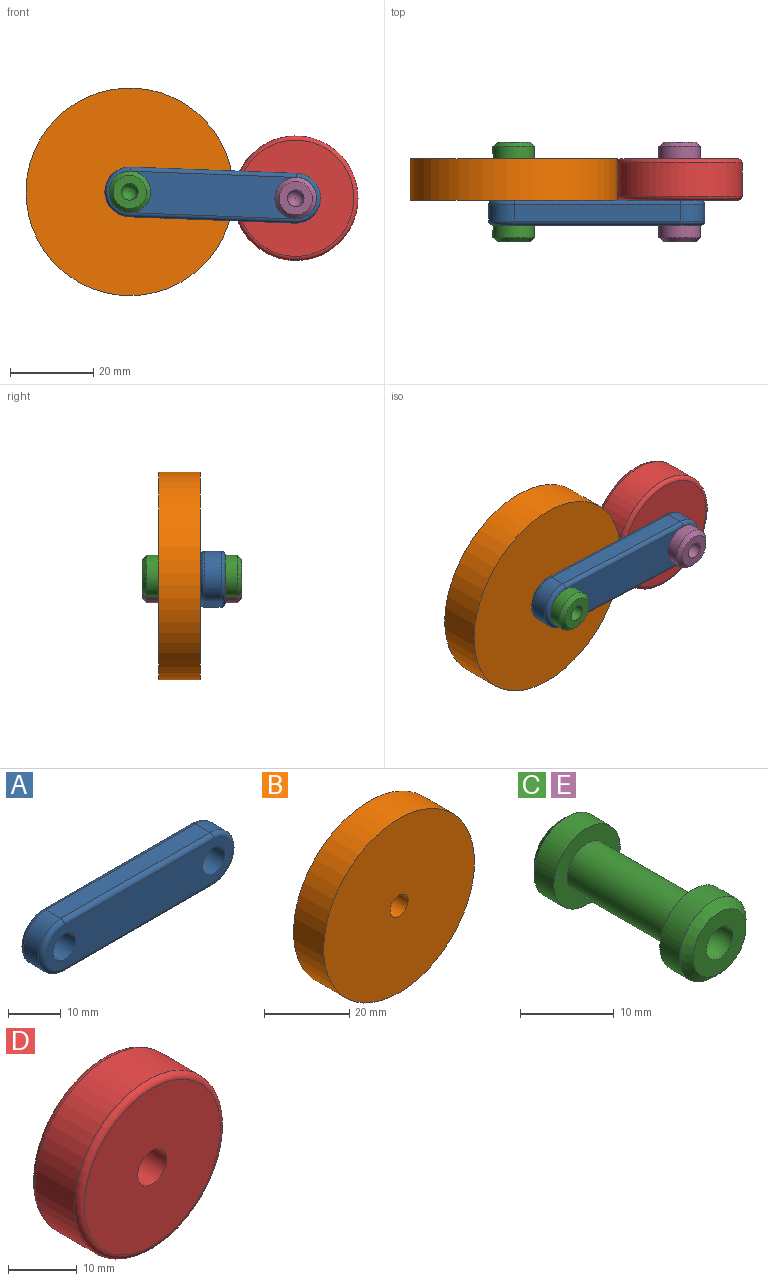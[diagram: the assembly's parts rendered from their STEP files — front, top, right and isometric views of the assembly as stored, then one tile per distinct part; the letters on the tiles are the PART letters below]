
ASSEMBLY  parts=5 mates=3
PART A: 16 faces, bbox 53x6x13 mm
  f0: plane 40x4mm, normal (0,0,1), area 160mm2, adj f1,f5,f8,f12
  f1: cylinder r=6mm len=12mm, axis (0,1,0), area 75.4mm2, adj f0,f2,f9,f13
  f2: plane 40x4mm, normal (0,0,-1), area 160mm2, adj f1,f5,f11,f15
  f3: cylinder r=3mm len=6mm, axis (0,1,0), area 113.1mm2, adj f6,f7
  f4: cylinder r=3mm len=6mm, axis (0,1,0), area 113.1mm2, adj f6,f7
  f5: cylinder r=6mm len=12mm, axis (0,1,0), area 75.4mm2, adj f0,f2,f10,f14
  f6: plane 50x10mm, normal (0,-1,0), area 422mm2, adj f3,f4,f12,f13,f14,f15
  f7: plane 50x10mm, normal (0,1,0), area 422mm2, adj f3,f4,f8,f9,f10,f11
  f8: cylinder r=1mm len=40mm, axis (-1,0,0), area 62.8mm2, adj f0,f7,f9,f10
  f9: torus R=5mm, axis (0,-1,0), area 27.8mm2, adj f1,f7,f8,f11
  f10: torus R=5mm, axis (0,-1,0), area 27.8mm2, adj f5,f7,f8,f11
  f11: cylinder r=1mm len=40mm, axis (1,0,0), area 62.8mm2, adj f2,f7,f9,f10
  f12: cylinder r=1mm len=40mm, axis (1,0,0), area 62.8mm2, adj f0,f6,f13,f14
  f13: torus R=5mm, axis (0,-1,0), area 27.8mm2, adj f1,f6,f12,f15
  f14: torus R=5mm, axis (0,-1,0), area 27.8mm2, adj f5,f6,f12,f15
  f15: cylinder r=1mm len=40mm, axis (-1,0,0), area 62.8mm2, adj f2,f6,f13,f14
PART B: 4 faces, bbox 50x10x50 mm
  f0: cylinder r=3mm len=10mm, axis (0,1,0), area 188.5mm2, adj f2,f3
  f1: cylinder r=25mm len=50mm, axis (0,1,0), area 1570.8mm2, adj f2,f3
  f2: plane 50x50mm, normal (0,-1,0), area 1935.2mm2, adj f0,f1
  f3: plane 50x50mm, normal (0,1,0), area 1935.2mm2, adj f0,f1
PART C: 11 faces, bbox 10x24x10 mm
  f0: cylinder r=3mm len=16mm, axis (0,-1,0), area 301.6mm2, adj f1,f8
  f1: plane 10x10mm, normal (0,1,0), area 50.3mm2, adj f0,f2
  f2: cylinder r=5mm len=10mm, axis (0,-1,0), area 94.2mm2, adj f1,f9
  f3: plane 8x8mm, normal (0,-1,0), area 37.7mm2, adj f4,f9
  f4: sphere r=2mm, area 25.1mm2, adj f3
  f5: sphere r=2mm, area 25.1mm2, adj f6
  f6: plane 8x8mm, normal (0,1,0), area 37.7mm2, adj f5,f10
  f7: cylinder r=5mm len=10mm, axis (0,-1,0), area 94.2mm2, adj f8,f10
  f8: plane 10x10mm, normal (0,-1,0), area 50.3mm2, adj f0,f7
  f9: cone r=4mm half-angle=45deg, axis (0,1,0), area 40mm2, adj f2,f3
  f10: cone r=5mm half-angle=45deg, axis (0,-1,0), area 40mm2, adj f6,f7
PART D: 6 faces, bbox 32.5x10x32.5 mm
  f0: cylinder r=3mm len=10mm, axis (0,1,0), area 188.5mm2, adj f2,f3
  f1: cylinder r=15mm len=30mm, axis (0,1,0), area 754mm2, adj f4,f5
  f2: plane 28x28mm, normal (0,-1,0), area 587.5mm2, adj f0,f5
  f3: plane 28x28mm, normal (0,1,0), area 587.5mm2, adj f0,f4
  f4: torus R=14mm, axis (0,-1,0), area 144.5mm2, adj f1,f3
  f5: torus R=14mm, axis (0,-1,0), area 144.5mm2, adj f1,f2
PART E: same geometry as C
PLACE A rot(axis=(0,1,0),2.2deg) t=(-3.45,-7.69,1.01)mm
PLACE B t=(1.32,2.31,-5.18)mm fixed
PLACE C t=(1.32,-5.69,-5.18)mm
PLACE D rot(axis=(0,1,0),2.2deg) t=(41.29,2.31,-6.7)mm
PLACE E rot(axis=(0,1,0),2.2deg) t=(41.29,-5.69,-6.7)mm
MATE revolute B.f1 <-> A.f1  axis (0,-1,0) through (1.32,-7.69,-5.18)mm
MATE fastened A.f4 <-> E.f0  axis (0,-1,0) through (41.29,-13.69,-6.7)mm
MATE fastened E.f0 <-> D.f0  axis (0,-1,0) through (41.29,2.31,-6.7)mm
